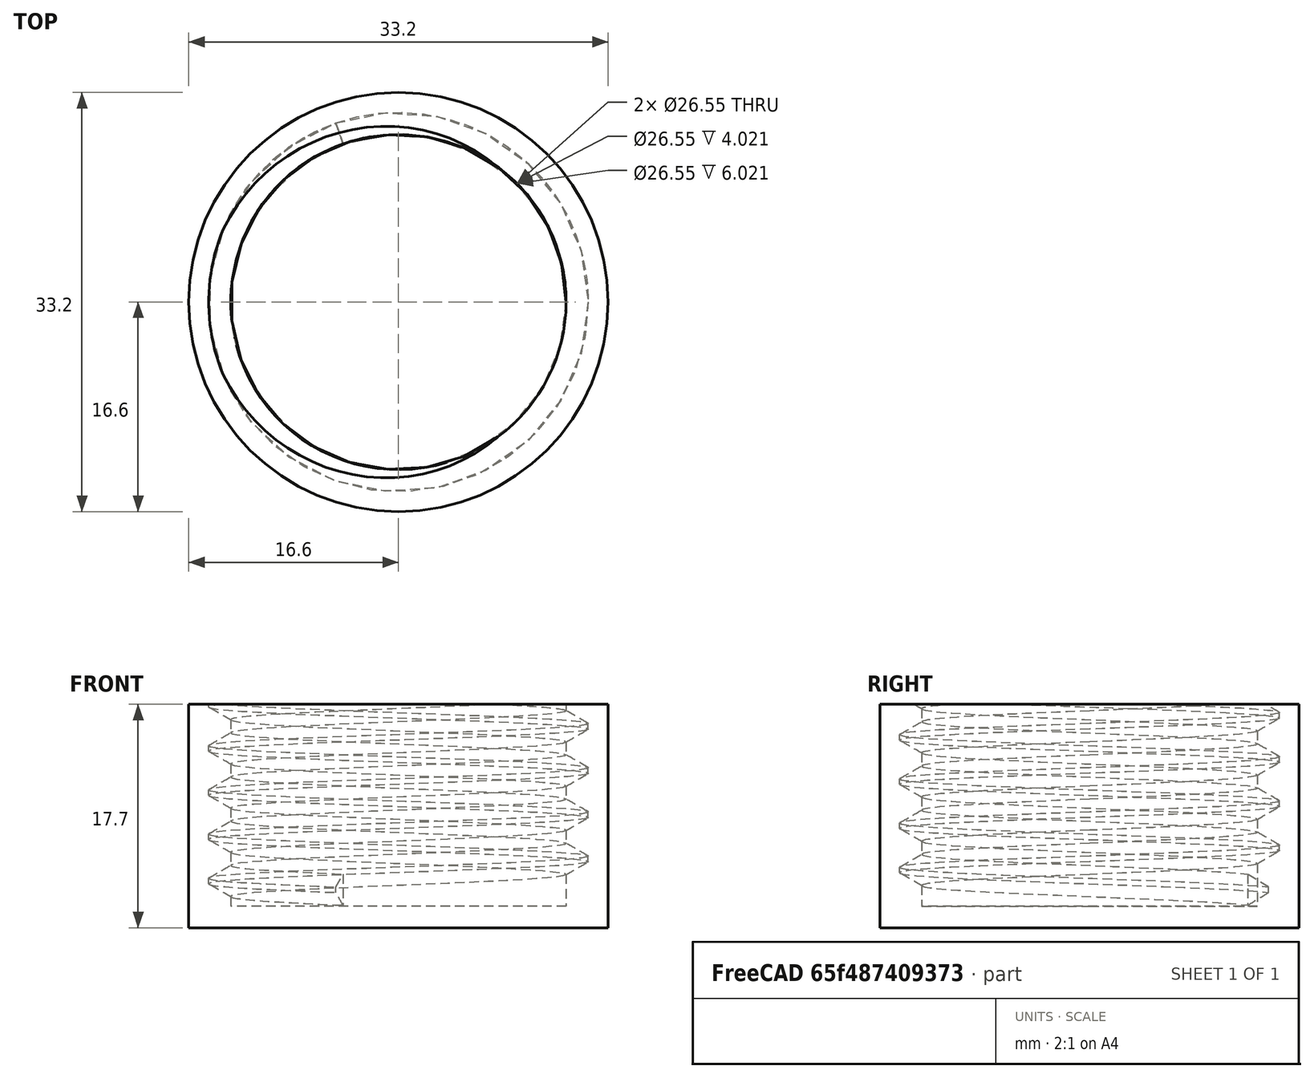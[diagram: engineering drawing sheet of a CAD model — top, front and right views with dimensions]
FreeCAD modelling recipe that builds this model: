
FCSTD DOCUMENT  (FreeCAD 0.22R35466 (Git))
Label: vasaline
License: Creative Commons Attribution 4.0
LicenseURL: https://creativecommons.org/licenses/by/4.0/
objects: PartDesign::AdditiveCylinder×1, PartDesign::Hole×1, PartDesign::Body×1
note: 5 computed .brp shape members not serialized (recipe doc carries the construction recipe); baked Part::Feature solids carry a one-line shape summary decoded from their .brp

FEATURE [PartDesign::AdditiveCylinder] Cylinder
  Angle = 360
  AttacherType = Attacher::AttachEngine3D
  FirstAngle = 0
  Height = 17.7
  Radius = 16.6
  SecondAngle = 0
  expr: Height = 17.7
  expr: Radius = 27.2 / 2 + 3
FEATURE [PartDesign::Hole] Hole
  BaseFeature = -> Cylinder
  CustomThreadClearance = 0
  Depth = 16
  DepthType = 0
  Diameter = 26.553
  DrillForDepth = false
  DrillPoint = 0
  DrillPointAngle = 118
  HoleCutCountersinkAngle = 90
  HoleCutCustomValues = false
  HoleCutDepth = 0
  HoleCutDiameter = 27.2
  HoleCutType = 0
  ModelThread = true
  Profile = -> Cylinder [Face3]
  Tapered = false
  TaperedAngle = 90
  ThreadClass = 0
  ThreadDepth = 16
  ThreadDepthType = 1
  ThreadDirection = 0
  ThreadFit = 0
  ThreadSize = 28
  ThreadType = 1
  Threaded = true
  UseCustomThreadClearance = false
FEATURE [PartDesign::Body] Body
  Group = -> [Cylinder,Hole]
  Origin = -> Origin
  Tip = -> Hole
